# Revit family: Loudspeaker_Bose_ArenaMatch-AM20_with U Bracket_1
name_source: partatom
category: Communication Devices
revit_build: Autodesk Revit 2015 (Build: 20160512_0715(x64)
units: mm (PartAtom-declared; Revit-internal decimal feet)

## types (3) — shared parameters
Bracket Material = Metal-Bose-Black
Crossover = 950 Hz internal passive or external bi-amp (Bose ControlSpace presets)
Default Elevation = 1219 mm
Depth = 417 mm
Description = Bose Professional ArenaMatch loudspeakers bring proven DeltaQ sound quality and flexibility to outdoor installations — sports stadiums, arenas, outdoor entertainment centers, and more.
Edition number = 1
Enviromental = Rated for direct-exposure outdoor installations (IEC 60529: IP55)
Frequency Range = 55 Hz to 18 kHz
Frequency Response = 65 Hz to 16 kHz
Grill Material = Grill-Bose-Black
HF Driver = 6 × Bose EMB2S titanium-diaphragm, neodymium compression drivers (2-inch voice coil)
Height = 437 mm
LF Driver = 1 × Bose LF14 neodymium 14-inch woofer (4-inch voice coil)
Manufacturer = Bose Professional
Model = ArenaMatch AM20
Mounting/Suspension = 8 × M12 threaded inserts (4 per side); 4 × M8 threaded inserts (2 per side)
Nominal Impedance = Passive: 8 Ω / Bi-amp: 8 Ω + 8 Ω
Power Connector = Barrier strips: passive in/through, bi-amp, and 70V/100V, with cover
Power Handling(Long-term continuous) = Bose Extended Lifecycle Test: LF - 600W, HF - 150W, Passive - 750W; AES Transducer Test: HF - 250W, LF - 1000W, HF - 250W, Passive - 1250W
Power Handling(peak) = Bose Extended Lifecycle Test 2: LF - 2400W, HF - 600W, Passive - 3000W; AES Transducer Test: HF - 250W, LF - 4000W, HF - 1000W, Passive - 5000W
Product Guid = 4344a2e1-7721-4bb6-b16a-b4f013c0100b
Product data url = https://bimobject.com
Recommended High-pass Filter = 60 Hz with minimum 12 dB / octave
Speaker Material = Matt-Bose-Black
Transformer Taps Information = 70V: 100, 200, 400 W; 100V: 200, 400 W
URL = https://pro.bose.com
Weight = 80.00 kg
Width = 782 mm

## per-type parameters (varying)
| type | Nominal Coverage Pattern | Nominal Sensitivity | Product code | Rated Maximum SPL |
| AM20/60 | 60° × 10° | LF: 94 dB, HF: 106 dB, Passive: 99 dB; | 794042-6660 | Calculated max. SPL @ 1 m (Bose power test) - LF: 122 dB, HF: 128 dB, Passive: 128 dB ; Calculated max. SPL @ 1 m (2-hour power test) - LF: 124 dB, HF: 130 dB, Passive: 130 dB ; Calculated max. SPL @ 1 m (Bose power test), peak - LF: 128 dB, HF: 134 dB, Passive: 134 dB; Calculated max. SPL @ 1 m (2-hour power test),
peak - LF: 130 dB, HF: 136 dB, Passive: 136 dB; |
| AM20/80 | 80° × 10° | LF: 94 dB, HF: 105 dB, Passive: 98 dB; | 794042-3360 | Calculated max. SPL @ 1 m (Bose power test) - LF: 122 dB, HF: 127 dB, Passive: 127 dB ; Calculated max. SPL @ 1 m (2-hour power test) - LF: 124 dB, HF: 129 dB, Passive: 129 dB ; Calculated max. SPL @ 1 m (Bose power test), peak - LF: 128 dB, HF: 133 dB, Passive: 133 dB; Calculated max. SPL @ 1 m (2-hour power test),
peak - LF: 130 dB, HF: 135 dB, Passive: 135 dB; |
| AM20/100 | 100° × 10° | LF: 94 dB, HF: 104 dB, Passive: 97 dB; | 794042-8860 | Calculated max. SPL @ 1 m (Bose power test) - LF: 122 dB, HF: 126 dB, Passive: 126 dB ; Calculated max. SPL @ 1 m (2-hour power test) - LF: 124 dB, HF: 129 dB, Passive: 129 dB ; Calculated max. SPL @ 1 m (Bose power test), peak - LF: 128 dB, HF: 133 dB, Passive: 133 dB; Calculated max. SPL @ 1 m (2-hour power test),
peak - LF: 130 dB, HF: 135 dB, Passive: 135 dB; |

## geometry (parser evidence)
native form markers: Blend x4, Sweep x11
no freeform markers — native parametric forms only
